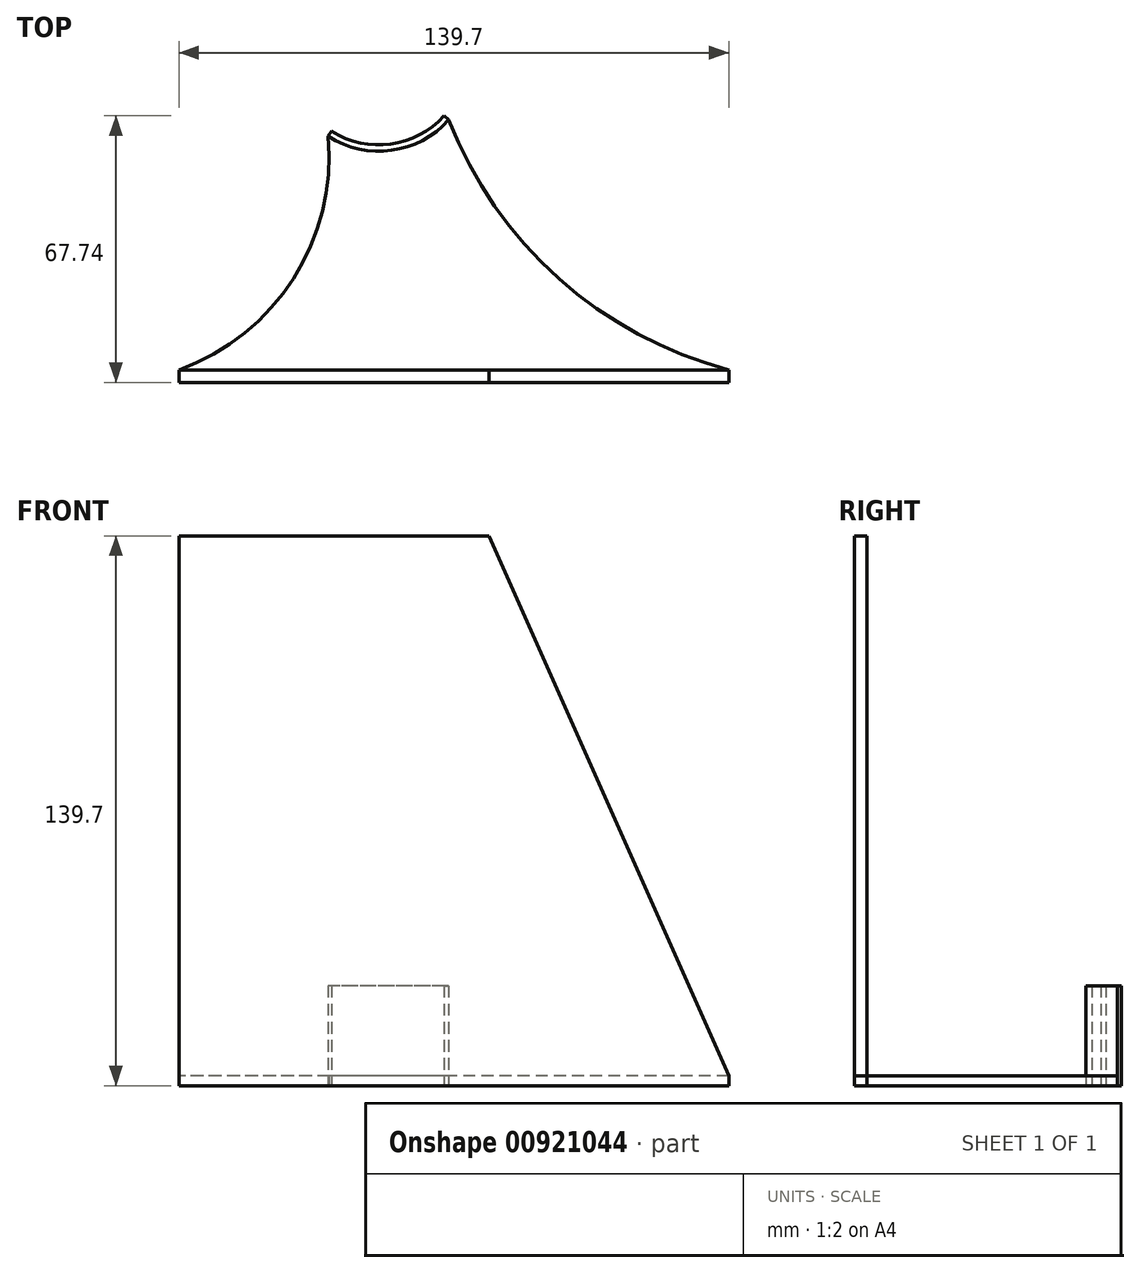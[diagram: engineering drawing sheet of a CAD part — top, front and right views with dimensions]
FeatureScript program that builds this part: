
annotation { "Feature Type Name" : "Feature", "Feature Type Description" : "" }
export const myFeature = defineFeature(function(context is Context, id is Id, definition is map)
    precondition{}
    {
        {
            var Q0;
            Q0=qCreatedBy(makeId("Front.planeOp"),FACE);
            var sketch = newSketch(context, id + "F0", { "sketchPlane" : qUnion([Q0])});
            skLineSegment(sketch, "E0", {"start": v(-48.17, -59.3) * mm, "end": v(-48.17, 80.4) * mm});
            skLineSegment(sketch, "E1", {"start": v(-48.17, 80.4) * mm, "end": v(30.57, 80.4) * mm});
            skLineSegment(sketch, "E2", {"start": v(91.53, -59.3) * mm, "end": v(-48.17, -59.3) * mm});
            skLineSegment(sketch, "E3", {"start": v(91.53, -59.3) * mm, "end": v(91.53, -56.76) * mm});
            skLineSegment(sketch, "E4", {"start": v(30.57, 80.4) * mm, "end": v(91.53, -56.76) * mm});
            skSolve(sketch);
        }
        {
            var Q0;
            Q0 = qSketchRegion(id + "F0", true);
            extrude(context, id + "F1", {"entities" : qUnion([Q0]), "depth" : 3.17 * mm, "offsetDistance" : 25.4 * mm});
        }
        {
            var Q0;
            Q0=makeQuery(id+"F1.opExtrude","SWEPT_FACE",FACE,{"disambiguationData":[OSD([sQuery(id+"F0.wireOp",EDGE,"E2")])]});
            var sketch = newSketch(context, id + "F2", { "sketchPlane" : qUnion([Q0])});
            skArc(sketch, "E5", {"start": v(19.2, -64.57) * mm, "mid": v(5.65, -57.36) * mm, "end": v(-9.35, -60.66) * mm});
            skArc(sketch, "E6", {"start": v(20.4, -63.52) * mm, "mid": v(5.86, -55.78) * mm, "end": v(-10.2, -59.32) * mm});
            skLineSegment(sketch, "E7", {"start": v(-9.35, -60.66) * mm, "end": v(-10.2, -59.32) * mm});
            skLineSegment(sketch, "E8", {"start": v(19.2, -64.57) * mm, "end": v(20.4, -63.52) * mm});
            skSolve(sketch);
        }
        {
            var Q0;
            Q0=makeQuery(id+"F2.imprint","IMPRINT",FACE,{"disambiguationData":[TD([[makeQuery(id+"F2.imprint","IMPRINT",EDGE,{"derivedFrom":sQuery(id+"F2.wireOp",EDGE,"E5")}),-1.0]])]});
            extrude(context, id + "F3", {"entities" : qUnion([Q0]), "oppositeDirection" : true, "depth" : 25.4 * mm, "offsetDistance" : 25.4 * mm});
        }
        {
            var Q0;
            Q0=makeQuery(id+"F1.opExtrude","SWEPT_FACE",FACE,{"disambiguationData":[OSD([sQuery(id+"F0.wireOp",EDGE,"E2")])]});
            var sketch = newSketch(context, id + "F4", { "sketchPlane" : qUnion([Q0])});
            skPoint(sketch, "E9.0", {"position": v(-48.17, 0) * mm});
            skPoint(sketch, "E10.0", {"position": v(-10.2, -59.32) * mm});
            skPoint(sketch, "E11.0", {"position": v(20.4, -63.52) * mm});
            skArc(sketch, "E12", {"start": v(-10.2, -59.32) * mm, "mid": v(-19.06, -23.18) * mm, "end": v(-48.17, 0) * mm});
            skLineSegment(sketch, "E13", {"start": v(-48.17, 0) * mm, "end": v(-48.17, 0) * mm});
            skArc(sketch, "E14.0", {"start": v(20.4, -63.52) * mm, "mid": v(5.86, -55.78) * mm, "end": v(-10.2, -59.32) * mm});
            skArc(sketch, "E15", {"start": v(91.53, 0) * mm, "mid": v(48.35, -23.23) * mm, "end": v(20.4, -63.52) * mm});
            skSolve(sketch);
        }
        {
            var Q0;
            Q0=makeQuery(id+"F4.imprint","IMPRINT",FACE,{"disambiguationData":[TD([[makeQuery(id+"F4.imprint","IMPRINT",EDGE,{"derivedFrom":sQuery(id+"F4.wireOp",EDGE,"E12")}),-1.0]])]});
            extrude(context, id + "F5", {"entities" : qUnion([Q0]), "oppositeDirection" : true, "depth" : 2.54 * mm, "offsetDistance" : 25.4 * mm});
        }
    });
